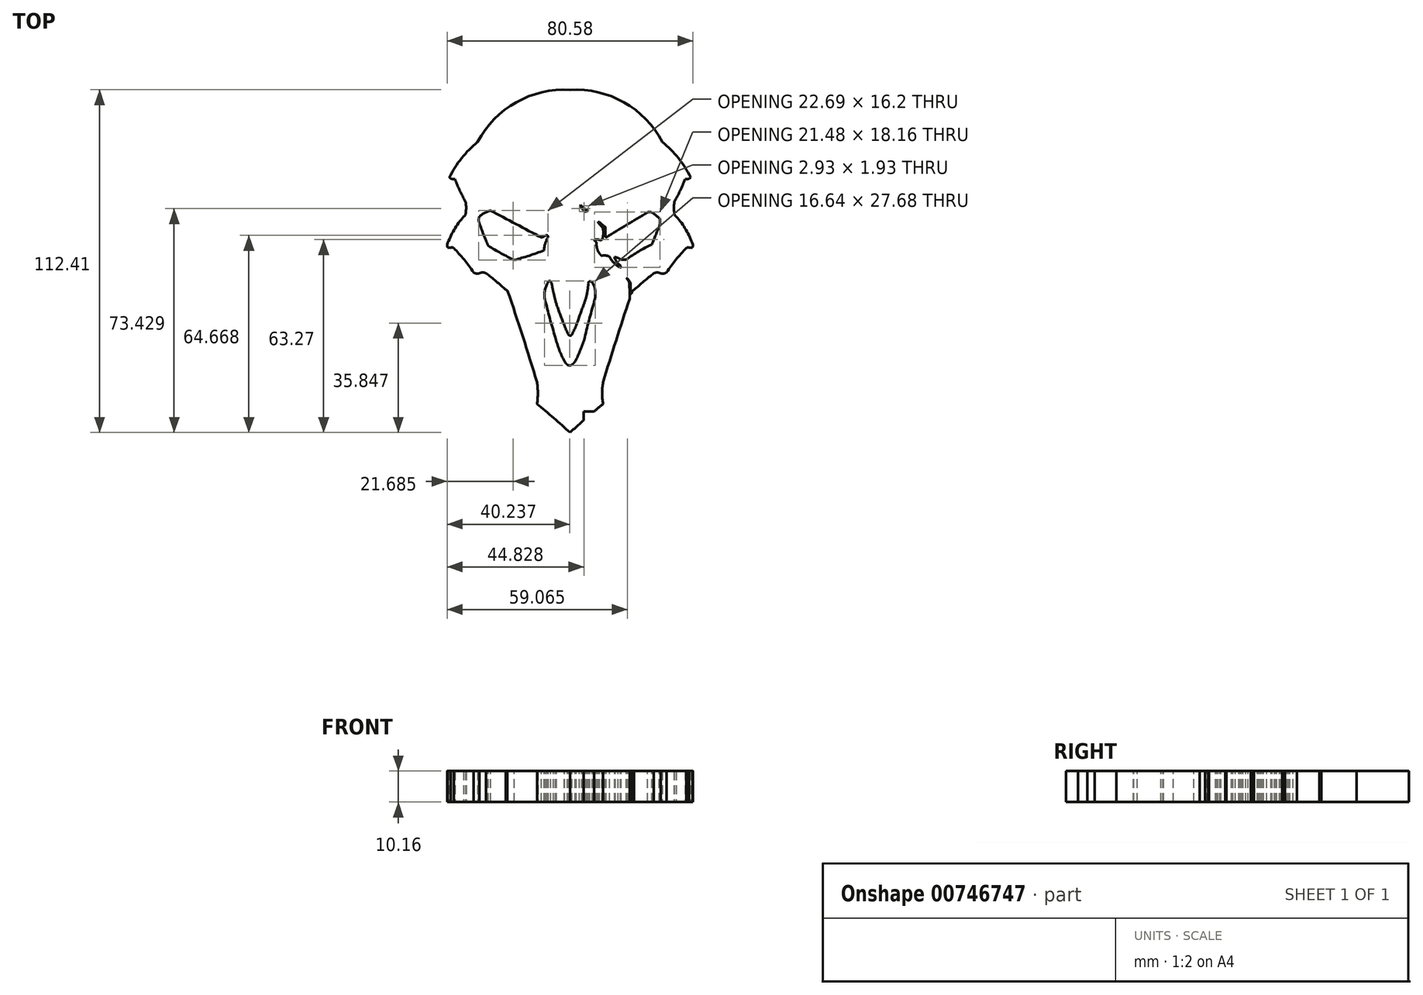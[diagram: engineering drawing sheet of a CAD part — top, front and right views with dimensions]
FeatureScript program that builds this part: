
annotation { "Feature Type Name" : "Feature", "Feature Type Description" : "" }
export const myFeature = defineFeature(function(context is Context, id is Id, definition is map)
    precondition{}
    {
        {
            var Q0;
            Q0=qCreatedBy(makeId("Top.planeOp"),FACE);
            var sketch = newSketch(context, id + "F0", { "sketchPlane" : qUnion([Q0])});
            skArc(sketch, "E0", {"start": v(-30.27, 46.68) * mm, "mid": v(-35.53, 41.4) * mm, "end": v(-39.5, 35.1) * mm});
            skArc(sketch, "E1", {"start": v(-39.5, 35.1) * mm, "mid": v(-38.7, 34.53) * mm, "end": v(-37.73, 34.53) * mm});
            skArc(sketch, "E2", {"start": v(-37.73, 34.53) * mm, "mid": v(-36.12, 30.74) * mm, "end": v(-34.24, 27.07) * mm});
            skArc(sketch, "E3", {"start": v(-34.24, 23.12) * mm, "mid": v(-34.05, 25.1) * mm, "end": v(-34.24, 27.07) * mm});
            skArc(sketch, "E4", {"start": v(-34.86, 22.24) * mm, "mid": v(-34.4, 22.58) * mm, "end": v(-34.24, 23.12) * mm});
            skArc(sketch, "E5", {"start": v(-38.1, 11.91) * mm, "mid": v(-38.57, 12.1) * mm, "end": v(-39.06, 12.04) * mm});
            skArc(sketch, "E6", {"start": v(-31.65, 3.94) * mm, "mid": v(-34.7, 8.07) * mm, "end": v(-38.1, 11.91) * mm});
            skArc(sketch, "E7", {"start": v(-34.86, 22.24) * mm, "mid": v(-38, 17.87) * mm, "end": v(-40.29, 12.99) * mm});
            skArc(sketch, "E8", {"start": v(-40.29, 12.99) * mm, "mid": v(-40.25, 12.5) * mm, "end": v(-40.1, 12.04) * mm});
            skArc(sketch, "E9", {"start": v(-40.1, 12.04) * mm, "mid": v(-39.58, 12.03) * mm, "end": v(-39.06, 12.04) * mm});
            skArc(sketch, "E10", {"start": v(-31.65, 3.94) * mm, "mid": v(-30.7, 3.53) * mm, "end": v(-29.68, 3.65) * mm});
            skArc(sketch, "E11", {"start": v(-27.5, 3.65) * mm, "mid": v(-28.59, 3.9) * mm, "end": v(-29.68, 3.65) * mm});
            skArc(sketch, "E12", {"start": v(-21.02, -1.81) * mm, "mid": v(-24.21, 0.97) * mm, "end": v(-27.5, 3.65) * mm});
            skArc(sketch, "E13", {"start": v(-20.5, -2.08) * mm, "mid": v(-20.73, -1.9) * mm, "end": v(-21.02, -1.81) * mm});
            skArc(sketch, "E14", {"start": v(-10.83, -32.15) * mm, "mid": v(-15.5, -17.06) * mm, "end": v(-20.5, -2.08) * mm});
            skArc(sketch, "E15", {"start": v(-10.83, -39.22) * mm, "mid": v(-10.55, -35.68) * mm, "end": v(-10.83, -32.15) * mm});
            skArc(sketch, "E16", {"start": v(0, -48.6) * mm, "mid": v(-5.35, -43.82) * mm, "end": v(-10.83, -39.22) * mm});
            skLineSegment(sketch, "E17", {"start": v(0, 63.77) * mm, "end": v(0, -48.6) * mm});
            skArc(sketch, "E18", {"start": v(0, 63.77) * mm, "mid": v(-17.65, 59.68) * mm, "end": v(-30.27, 46.68) * mm});
            skSolve(sketch);
        }
        {
            var Q0;
            Q0=qSketchRegion(id+"F0",true);
            extrude(context, id + "F1", {"entities" : qUnion([Q0]), "depth" : 10.16 * mm, "offsetDistance" : 25.4 * mm});
        }
        {
            var Q0;
            Q0=makeQuery(id+"F1.opExtrude","SWEPT_BODY",BODY,{"disambiguationData":[OSD([sQuery(id+"F0.wireOp",EDGE,"E0"),sQuery(id+"F0.wireOp",EDGE,"E1"),sQuery(id+"F0.wireOp",EDGE,"E2"),sQuery(id+"F0.wireOp",EDGE,"E3"),sQuery(id+"F0.wireOp",EDGE,"E4"),sQuery(id+"F0.wireOp",EDGE,"E5"),sQuery(id+"F0.wireOp",EDGE,"E6"),sQuery(id+"F0.wireOp",EDGE,"E7"),sQuery(id+"F0.wireOp",EDGE,"E8"),sQuery(id+"F0.wireOp",EDGE,"E9"),sQuery(id+"F0.wireOp",EDGE,"E10"),sQuery(id+"F0.wireOp",EDGE,"E11"),sQuery(id+"F0.wireOp",EDGE,"E12"),sQuery(id+"F0.wireOp",EDGE,"E13"),sQuery(id+"F0.wireOp",EDGE,"E14"),sQuery(id+"F0.wireOp",EDGE,"E15"),sQuery(id+"F0.wireOp",EDGE,"E16"),sQuery(id+"F0.wireOp",EDGE,"E17"),sQuery(id+"F0.wireOp",EDGE,"E18")])]});
            var Q1;
            Q1=qCreatedBy(makeId("Right.planeOp"),FACE);
            mirror(context, id + "F2", {"operationType" : NewBodyOperationType.ADD, "entities" : qUnion([Q0]), "mirrorPlane" : qUnion([Q1])});
        }
        {
            var Q0;
            {var subQ0=makeQuery(id+"F1.opExtrude","CAP_FACE",FACE,{"disambiguationData":[OSD([sQuery(id+"F0.wireOp",EDGE,"E0"),sQuery(id+"F0.wireOp",EDGE,"E1"),sQuery(id+"F0.wireOp",EDGE,"E2"),sQuery(id+"F0.wireOp",EDGE,"E3"),sQuery(id+"F0.wireOp",EDGE,"E4"),sQuery(id+"F0.wireOp",EDGE,"E5"),sQuery(id+"F0.wireOp",EDGE,"E6"),sQuery(id+"F0.wireOp",EDGE,"E7"),sQuery(id+"F0.wireOp",EDGE,"E8"),sQuery(id+"F0.wireOp",EDGE,"E9"),sQuery(id+"F0.wireOp",EDGE,"E10"),sQuery(id+"F0.wireOp",EDGE,"E11"),sQuery(id+"F0.wireOp",EDGE,"E12"),sQuery(id+"F0.wireOp",EDGE,"E13"),sQuery(id+"F0.wireOp",EDGE,"E14"),sQuery(id+"F0.wireOp",EDGE,"E15"),sQuery(id+"F0.wireOp",EDGE,"E16"),sQuery(id+"F0.wireOp",EDGE,"E17"),sQuery(id+"F0.wireOp",EDGE,"E18")])],"isStart":false});Q0=makeQuery(id+"F2.boolean.opBoolean","MERGE",FACE,{"derivedFrom":[subQ0,makeQuery(id+"F2.opPattern","COPY",FACE,{"derivedFrom":subQ0,"instanceName":"1"})]});}
            var sketch = newSketch(context, id + "F3", { "sketchPlane" : qUnion([Q0])});
            skArc(sketch, "E19", {"start": v(-26, 24.18) * mm, "mid": v(-17.72, 19.77) * mm, "end": v(-9.44, 15.37) * mm});
            skArc(sketch, "E20", {"start": v(-9.44, 15.37) * mm, "mid": v(-8.67, 15.65) * mm, "end": v(-7.94, 16.04) * mm});
            skArc(sketch, "E21", {"start": v(-26.76, 12.61) * mm, "mid": v(-22.58, 10.17) * mm, "end": v(-18.26, 7.98) * mm});
            skArc(sketch, "E22", {"start": v(-29.69, 20.03) * mm, "mid": v(-28.33, 16.28) * mm, "end": v(-26.76, 12.61) * mm});
            skArc(sketch, "E23", {"start": v(-29.69, 22.27) * mm, "mid": v(-29.95, 21.15) * mm, "end": v(-29.69, 20.03) * mm});
            skArc(sketch, "E24", {"start": v(-26, 24.18) * mm, "mid": v(-27.96, 23.44) * mm, "end": v(-29.69, 22.27) * mm});
            skArc(sketch, "E25", {"start": v(-7.58, 16.16) * mm, "mid": v(-7.77, 16.1) * mm, "end": v(-7.94, 16.04) * mm});
            skArc(sketch, "E26", {"start": v(-7.58, 16.16) * mm, "mid": v(-7.47, 16.14) * mm, "end": v(-7.35, 16.16) * mm});
            skArc(sketch, "E27", {"start": v(-7.28, 15.37) * mm, "mid": v(-7.26, 15.77) * mm, "end": v(-7.35, 16.16) * mm});
            skArc(sketch, "E28", {"start": v(-7.28, 15.37) * mm, "mid": v(-8.16, 13.31) * mm, "end": v(-8.55, 11.1) * mm});
            skArc(sketch, "E29", {"start": v(-18.26, 7.98) * mm, "mid": v(-13.36, 9.42) * mm, "end": v(-8.55, 11.1) * mm});
            skSolve(sketch);
        }
        {
            var Q0;
            Q0=qSketchRegion(id+"F3",true);
            extrude(context, id + "F4", {"entities" : qUnion([Q0]), "operationType" : NewBodyOperationType.REMOVE, "oppositeDirection" : true, "depth" : 25.4 * mm, "offsetDistance" : 25.4 * mm});
        }
        {
            var Q0;
            {var subQ0=makeQuery(id+"F1.opExtrude","CAP_FACE",FACE,{"disambiguationData":[OSD([sQuery(id+"F0.wireOp",EDGE,"E0"),sQuery(id+"F0.wireOp",EDGE,"E1"),sQuery(id+"F0.wireOp",EDGE,"E2"),sQuery(id+"F0.wireOp",EDGE,"E3"),sQuery(id+"F0.wireOp",EDGE,"E4"),sQuery(id+"F0.wireOp",EDGE,"E5"),sQuery(id+"F0.wireOp",EDGE,"E6"),sQuery(id+"F0.wireOp",EDGE,"E7"),sQuery(id+"F0.wireOp",EDGE,"E8"),sQuery(id+"F0.wireOp",EDGE,"E9"),sQuery(id+"F0.wireOp",EDGE,"E10"),sQuery(id+"F0.wireOp",EDGE,"E11"),sQuery(id+"F0.wireOp",EDGE,"E12"),sQuery(id+"F0.wireOp",EDGE,"E13"),sQuery(id+"F0.wireOp",EDGE,"E14"),sQuery(id+"F0.wireOp",EDGE,"E15"),sQuery(id+"F0.wireOp",EDGE,"E16"),sQuery(id+"F0.wireOp",EDGE,"E17"),sQuery(id+"F0.wireOp",EDGE,"E18")])],"isStart":false});Q0=makeQuery(id+"F2.boolean.opBoolean","MERGE",FACE,{"derivedFrom":[subQ0,makeQuery(id+"F2.opPattern","COPY",FACE,{"derivedFrom":subQ0,"instanceName":"1"})]});}
            var sketch = newSketch(context, id + "F5", { "sketchPlane" : qUnion([Q0])});
            skArc(sketch, "E30", {"start": v(25.42, 23.61) * mm, "mid": v(18.6, 19.55) * mm, "end": v(11.87, 15.37) * mm});
            skArc(sketch, "E31", {"start": v(26.78, 23.61) * mm, "mid": v(26.1, 23.76) * mm, "end": v(25.42, 23.61) * mm});
            skArc(sketch, "E32", {"start": v(29.26, 21.73) * mm, "mid": v(28.05, 22.71) * mm, "end": v(26.78, 23.61) * mm});
            skArc(sketch, "E33", {"start": v(29.5, 21.39) * mm, "mid": v(29.4, 21.57) * mm, "end": v(29.26, 21.73) * mm});
            skArc(sketch, "E34", {"start": v(29.5, 19.76) * mm, "mid": v(29.51, 20.58) * mm, "end": v(29.5, 21.39) * mm});
            skArc(sketch, "E35", {"start": v(26.78, 13.08) * mm, "mid": v(28.17, 16.4) * mm, "end": v(29.5, 19.76) * mm});
            skArc(sketch, "E36", {"start": v(26.78, 13.08) * mm, "mid": v(22.49, 10.8) * mm, "end": v(18.43, 8.13) * mm});
            skArc(sketch, "E37", {"start": v(16.8, 8.13) * mm, "mid": v(17.62, 8.07) * mm, "end": v(18.43, 8.13) * mm});
            skArc(sketch, "E38", {"start": v(16.8, 8.13) * mm, "mid": v(15.76, 8.64) * mm, "end": v(14.65, 8.96) * mm});
            skArc(sketch, "E39", {"start": v(12.98, 9) * mm, "mid": v(13.7, 7.88) * mm, "end": v(14.58, 6.88) * mm});
            skArc(sketch, "E40", {"start": v(12.1, 9.4) * mm, "mid": v(11.24, 9.46) * mm, "end": v(10.38, 9.4) * mm});
            skArc(sketch, "E41", {"start": v(9.5, 10.35) * mm, "mid": v(9.88, 9.82) * mm, "end": v(10.38, 9.4) * mm});
            skArc(sketch, "E42", {"start": v(8.7, 13.2) * mm, "mid": v(8.88, 11.72) * mm, "end": v(9.5, 10.35) * mm});
            skArc(sketch, "E43", {"start": v(8.7, 13.2) * mm, "mid": v(8.63, 13.72) * mm, "end": v(8.25, 14.08) * mm});
            skArc(sketch, "E44", {"start": v(8.07, 14.36) * mm, "mid": v(8.15, 14.2) * mm, "end": v(8.25, 14.08) * mm});
            skArc(sketch, "E45", {"start": v(8.07, 14.73) * mm, "mid": v(8.03, 14.54) * mm, "end": v(8.07, 14.36) * mm});
            skArc(sketch, "E46", {"start": v(14.9, 8.09) * mm, "mid": v(15.57, 7) * mm, "end": v(16.55, 6.16) * mm});
            skArc(sketch, "E47", {"start": v(16.55, 6.16) * mm, "mid": v(16.6, 5.84) * mm, "end": v(16.84, 5.6) * mm});
            skArc(sketch, "E48", {"start": v(15.76, 5.9) * mm, "mid": v(16.27, 5.66) * mm, "end": v(16.84, 5.6) * mm});
            skArc(sketch, "E49", {"start": v(14.58, 6.88) * mm, "mid": v(15.14, 6.35) * mm, "end": v(15.76, 5.9) * mm});
            skArc(sketch, "E50", {"start": v(10.45, 14.6) * mm, "mid": v(10.58, 14.76) * mm, "end": v(10.64, 14.94) * mm});
            skArc(sketch, "E51", {"start": v(10.64, 14.94) * mm, "mid": v(10.87, 16.03) * mm, "end": v(10.9, 17.14) * mm});
            skArc(sketch, "E52", {"start": v(10.9, 17.14) * mm, "mid": v(10.85, 17.89) * mm, "end": v(10.64, 18.61) * mm});
            skArc(sketch, "E53", {"start": v(10.64, 18.61) * mm, "mid": v(10, 19.4) * mm, "end": v(9.28, 20.13) * mm});
            skArc(sketch, "E54", {"start": v(9.2, 20.42) * mm, "mid": v(9.22, 20.27) * mm, "end": v(9.28, 20.13) * mm});
            skArc(sketch, "E55", {"start": v(9.2, 20.42) * mm, "mid": v(9.46, 20.35) * mm, "end": v(9.72, 20.42) * mm});
            skArc(sketch, "E56", {"start": v(9.72, 20.42) * mm, "mid": v(10.53, 19.58) * mm, "end": v(11.48, 18.92) * mm});
            skArc(sketch, "E57", {"start": v(11.59, 18.76) * mm, "mid": v(11.55, 18.85) * mm, "end": v(11.48, 18.92) * mm});
            skArc(sketch, "E58", {"start": v(11.74, 15.48) * mm, "mid": v(11.78, 15.4) * mm, "end": v(11.87, 15.37) * mm});
            skArc(sketch, "E59", {"start": v(11.59, 18.76) * mm, "mid": v(11.54, 17.12) * mm, "end": v(11.74, 15.48) * mm});
            skArc(sketch, "E60", {"start": v(9.51, 14.6) * mm, "mid": v(9.98, 14.5) * mm, "end": v(10.45, 14.6) * mm});
            skArc(sketch, "E61", {"start": v(9.51, 14.6) * mm, "mid": v(9.27, 14.67) * mm, "end": v(9.02, 14.7) * mm});
            skArc(sketch, "E62", {"start": v(8.48, 14.71) * mm, "mid": v(8.75, 14.65) * mm, "end": v(9.02, 14.7) * mm});
            skArc(sketch, "E63", {"start": v(8.07, 14.73) * mm, "mid": v(8.27, 14.69) * mm, "end": v(8.48, 14.71) * mm});
            skArc(sketch, "E64", {"start": v(14.65, 8.96) * mm, "mid": v(14.6, 8.78) * mm, "end": v(14.65, 8.6) * mm});
            skArc(sketch, "E65", {"start": v(14.65, 8.6) * mm, "mid": v(14.76, 8.34) * mm, "end": v(14.9, 8.09) * mm});
            skArc(sketch, "E66", {"start": v(12.98, 9) * mm, "mid": v(12.57, 9.26) * mm, "end": v(12.1, 9.4) * mm});
            skSolve(sketch);
        }
        {
            var Q0;
            Q0=qSketchRegion(id+"F5",true);
            extrude(context, id + "F6", {"entities" : qUnion([Q0]), "operationType" : NewBodyOperationType.REMOVE, "oppositeDirection" : true, "depth" : 25.4 * mm, "offsetDistance" : 25.4 * mm});
        }
        {
            var Q0;
            Q0=qSketchRegion(id+"F5",true);
            extrude(context, id + "F7", {"entities" : qUnion([Q0]), "operationType" : NewBodyOperationType.REMOVE, "oppositeDirection" : true, "depth" : 25.4 * mm, "offsetDistance" : 25.4 * mm});
        }
        {
            var Q0;
            {var subQ0=makeQuery(id+"F1.opExtrude","CAP_FACE",FACE,{"disambiguationData":[OSD([sQuery(id+"F0.wireOp",EDGE,"E0"),sQuery(id+"F0.wireOp",EDGE,"E1"),sQuery(id+"F0.wireOp",EDGE,"E2"),sQuery(id+"F0.wireOp",EDGE,"E3"),sQuery(id+"F0.wireOp",EDGE,"E4"),sQuery(id+"F0.wireOp",EDGE,"E5"),sQuery(id+"F0.wireOp",EDGE,"E6"),sQuery(id+"F0.wireOp",EDGE,"E7"),sQuery(id+"F0.wireOp",EDGE,"E8"),sQuery(id+"F0.wireOp",EDGE,"E9"),sQuery(id+"F0.wireOp",EDGE,"E10"),sQuery(id+"F0.wireOp",EDGE,"E11"),sQuery(id+"F0.wireOp",EDGE,"E12"),sQuery(id+"F0.wireOp",EDGE,"E13"),sQuery(id+"F0.wireOp",EDGE,"E14"),sQuery(id+"F0.wireOp",EDGE,"E15"),sQuery(id+"F0.wireOp",EDGE,"E16"),sQuery(id+"F0.wireOp",EDGE,"E17"),sQuery(id+"F0.wireOp",EDGE,"E18")])],"isStart":false});Q0=makeQuery(id+"F2.boolean.opBoolean","MERGE",FACE,{"derivedFrom":[subQ0,makeQuery(id+"F2.opPattern","COPY",FACE,{"derivedFrom":subQ0,"instanceName":"1"})]});}
            var sketch = newSketch(context, id + "F8", { "sketchPlane" : qUnion([Q0])});
            skArc(sketch, "E67", {"start": v(19.58, -4.75) * mm, "mid": v(19.54, -2.14) * mm, "end": v(19.42, 0.46) * mm});
            skArc(sketch, "E68", {"start": v(19.42, 0.46) * mm, "mid": v(19.15, 1.16) * mm, "end": v(18.68, 1.76) * mm});
            skArc(sketch, "E69", {"start": v(18.68, 2) * mm, "mid": v(18.66, 1.88) * mm, "end": v(18.68, 1.76) * mm});
            skArc(sketch, "E70", {"start": v(18.75, 2.17) * mm, "mid": v(18.7, 2.1) * mm, "end": v(18.68, 2) * mm});
            skArc(sketch, "E71", {"start": v(18.75, 2.17) * mm, "mid": v(18.8, 1.91) * mm, "end": v(19, 1.74) * mm});
            skArc(sketch, "E72", {"start": v(19.78, 0.52) * mm, "mid": v(19.41, 1.15) * mm, "end": v(19, 1.74) * mm});
            skArc(sketch, "E73", {"start": v(19.78, 0.52) * mm, "mid": v(19.85, -1.26) * mm, "end": v(20.03, -3.02) * mm});
            skArc(sketch, "E74", {"start": v(20.03, -3.02) * mm, "mid": v(20.05, -3.06) * mm, "end": v(20.08, -3.08) * mm});
            skArc(sketch, "E75", {"start": v(20.08, -3.08) * mm, "mid": v(20.16, -3.07) * mm, "end": v(20.22, -3) * mm});
            skArc(sketch, "E76", {"start": v(19.58, -4.75) * mm, "mid": v(24.58, -5.6) * mm, "end": v(20.22, -3) * mm});
            skSolve(sketch);
        }
        {
            var Q0;
            {var subQ0=makeQuery(id+"F1.opExtrude","CAP_FACE",FACE,{"disambiguationData":[OSD([sQuery(id+"F0.wireOp",EDGE,"E0"),sQuery(id+"F0.wireOp",EDGE,"E1"),sQuery(id+"F0.wireOp",EDGE,"E2"),sQuery(id+"F0.wireOp",EDGE,"E3"),sQuery(id+"F0.wireOp",EDGE,"E4"),sQuery(id+"F0.wireOp",EDGE,"E5"),sQuery(id+"F0.wireOp",EDGE,"E6"),sQuery(id+"F0.wireOp",EDGE,"E7"),sQuery(id+"F0.wireOp",EDGE,"E8"),sQuery(id+"F0.wireOp",EDGE,"E9"),sQuery(id+"F0.wireOp",EDGE,"E10"),sQuery(id+"F0.wireOp",EDGE,"E11"),sQuery(id+"F0.wireOp",EDGE,"E12"),sQuery(id+"F0.wireOp",EDGE,"E13"),sQuery(id+"F0.wireOp",EDGE,"E14"),sQuery(id+"F0.wireOp",EDGE,"E15"),sQuery(id+"F0.wireOp",EDGE,"E16"),sQuery(id+"F0.wireOp",EDGE,"E17"),sQuery(id+"F0.wireOp",EDGE,"E18")])],"isStart":false});Q0=makeQuery(id+"F2.boolean.opBoolean","MERGE",FACE,{"derivedFrom":[subQ0,makeQuery(id+"F2.opPattern","COPY",FACE,{"derivedFrom":subQ0,"instanceName":"1"})]});}
            var sketch = newSketch(context, id + "F9", { "sketchPlane" : qUnion([Q0])});
            skArc(sketch, "E77", {"start": v(3.88, 25.76) * mm, "mid": v(4.36, 25.2) * mm, "end": v(4.93, 24.73) * mm});
            skArc(sketch, "E78", {"start": v(4.93, 24.73) * mm, "mid": v(5.45, 24.54) * mm, "end": v(6, 24.5) * mm});
            skArc(sketch, "E79", {"start": v(4.68, 23.9) * mm, "mid": v(4.97, 23.88) * mm, "end": v(5.26, 23.9) * mm});
            skArc(sketch, "E80", {"start": v(4.68, 23.9) * mm, "mid": v(3.93, 24.9) * mm, "end": v(3.07, 25.8) * mm});
            skArc(sketch, "E81", {"start": v(3.07, 25.8) * mm, "mid": v(3.47, 25.74) * mm, "end": v(3.88, 25.76) * mm});
            skArc(sketch, "E82", {"start": v(6, 24.5) * mm, "mid": v(5.8, 24.24) * mm, "end": v(5.69, 23.95) * mm});
            skArc(sketch, "E83", {"start": v(5.69, 23.95) * mm, "mid": v(5.47, 23.94) * mm, "end": v(5.26, 23.9) * mm});
            skSolve(sketch);
        }
        {
            var Q0;
            Q0=qSketchRegion(id+"F9",true);
            extrude(context, id + "F10", {"entities" : qUnion([Q0]), "operationType" : NewBodyOperationType.REMOVE, "oppositeDirection" : true, "depth" : 25.4 * mm, "offsetDistance" : 25.4 * mm});
        }
        {
            var Q0;
            {var subQ20=sQuery(id+"F8.wireOp",EDGE,"E67");Q0=makeQuery(id+"F8.imprint","IMPRINT",FACE,{"disambiguationData":[TD([[makeQuery(id+"F8.imprint","IMPRINT",EDGE,{"derivedFrom":subQ20}),1.0]])]});}
            var sketch = newSketch(context, id + "F11", { "sketchPlane" : qUnion([Q0])});
            skArc(sketch, "E84", {"start": v(-6.35, 0.89) * mm, "mid": v(-6.69, 1.1) * mm, "end": v(-7.05, 0.93) * mm});
            skArc(sketch, "E85", {"start": v(-7.05, 0.93) * mm, "mid": v(-8.21, -1.83) * mm, "end": v(-8.25, -4.82) * mm});
            skArc(sketch, "E86", {"start": v(-8.25, -4.82) * mm, "mid": v(-6.62, -11.16) * mm, "end": v(-4.78, -17.44) * mm});
            skArc(sketch, "E87", {"start": v(-4.78, -17.44) * mm, "mid": v(-3.54, -21.47) * mm, "end": v(-1.75, -25.28) * mm});
            skArc(sketch, "E88", {"start": v(-1.75, -25.28) * mm, "mid": v(-1.37, -25.86) * mm, "end": v(-0.9, -26.35) * mm});
            skArc(sketch, "E89", {"start": v(-0.9, -26.35) * mm, "mid": v(-0.13, -26.59) * mm, "end": v(0.64, -26.35) * mm});
            skArc(sketch, "E90", {"start": v(0.64, -26.35) * mm, "mid": v(1.2, -25.84) * mm, "end": v(1.7, -25.28) * mm});
            skArc(sketch, "E91", {"start": v(1.7, -25.28) * mm, "mid": v(3.44, -21.43) * mm, "end": v(4.85, -17.44) * mm});
            skArc(sketch, "E92", {"start": v(8.19, -4.82) * mm, "mid": v(6.4, -11.1) * mm, "end": v(4.85, -17.44) * mm});
            skArc(sketch, "E93", {"start": v(8.19, -4.82) * mm, "mid": v(8.27, -3.16) * mm, "end": v(8.19, -1.5) * mm});
            skArc(sketch, "E94", {"start": v(8.19, -1.5) * mm, "mid": v(7.82, -0.38) * mm, "end": v(7.27, 0.67) * mm});
            skArc(sketch, "E95", {"start": v(7.27, 0.67) * mm, "mid": v(6.93, 0.9) * mm, "end": v(6.55, 1.01) * mm});
            skArc(sketch, "E96", {"start": v(5.65, -2.47) * mm, "mid": v(5.9, -1.06) * mm, "end": v(5.93, 0.36) * mm});
            skArc(sketch, "E97", {"start": v(4.5, -6.68) * mm, "mid": v(5.18, -4.6) * mm, "end": v(5.65, -2.47) * mm});
            skArc(sketch, "E98", {"start": v(4.5, -6.68) * mm, "mid": v(3.23, -10.02) * mm, "end": v(2.08, -13.4) * mm});
            skArc(sketch, "E99", {"start": v(0.57, -16.55) * mm, "mid": v(1.35, -14.98) * mm, "end": v(2.08, -13.4) * mm});
            skArc(sketch, "E100", {"start": v(-0.45, -16.55) * mm, "mid": v(0.06, -16.81) * mm, "end": v(0.57, -16.55) * mm});
            skArc(sketch, "E101", {"start": v(-1.88, -13.4) * mm, "mid": v(-1.23, -15) * mm, "end": v(-0.45, -16.55) * mm});
            skArc(sketch, "E102", {"start": v(-4.4, -6.68) * mm, "mid": v(-3.18, -10.05) * mm, "end": v(-1.88, -13.4) * mm});
            skArc(sketch, "E103", {"start": v(-5.5, -2.47) * mm, "mid": v(-4.97, -4.58) * mm, "end": v(-4.4, -6.68) * mm});
            skArc(sketch, "E104", {"start": v(-5.97, -0.02) * mm, "mid": v(-5.74, -1.24) * mm, "end": v(-5.5, -2.47) * mm});
            skArc(sketch, "E105", {"start": v(-5.97, -0.02) * mm, "mid": v(-6.1, 0.46) * mm, "end": v(-6.35, 0.89) * mm});
            skArc(sketch, "E106", {"start": v(6.55, 1.01) * mm, "mid": v(6.15, 0.77) * mm, "end": v(5.93, 0.36) * mm});
            skSolve(sketch);
        }
        {
            var Q0;
            Q0=qSketchRegion(id+"F11",true);
            extrude(context, id + "F12", {"entities" : qUnion([Q0]), "operationType" : NewBodyOperationType.REMOVE, "oppositeDirection" : true, "depth" : 25.4 * mm, "offsetDistance" : 25.4 * mm});
        }
        {
            var Q0;
            {var subQ0=makeQuery(id+"F1.opExtrude","CAP_FACE",FACE,{"disambiguationData":[OSD([sQuery(id+"F0.wireOp",EDGE,"E0"),sQuery(id+"F0.wireOp",EDGE,"E1"),sQuery(id+"F0.wireOp",EDGE,"E2"),sQuery(id+"F0.wireOp",EDGE,"E3"),sQuery(id+"F0.wireOp",EDGE,"E4"),sQuery(id+"F0.wireOp",EDGE,"E5"),sQuery(id+"F0.wireOp",EDGE,"E6"),sQuery(id+"F0.wireOp",EDGE,"E7"),sQuery(id+"F0.wireOp",EDGE,"E8"),sQuery(id+"F0.wireOp",EDGE,"E9"),sQuery(id+"F0.wireOp",EDGE,"E10"),sQuery(id+"F0.wireOp",EDGE,"E11"),sQuery(id+"F0.wireOp",EDGE,"E12"),sQuery(id+"F0.wireOp",EDGE,"E13"),sQuery(id+"F0.wireOp",EDGE,"E14"),sQuery(id+"F0.wireOp",EDGE,"E15"),sQuery(id+"F0.wireOp",EDGE,"E16"),sQuery(id+"F0.wireOp",EDGE,"E17"),sQuery(id+"F0.wireOp",EDGE,"E18")])],"isStart":false});Q0=makeQuery(id+"F2.boolean.opBoolean","MERGE",FACE,{"derivedFrom":[subQ0,makeQuery(id+"F2.opPattern","COPY",FACE,{"derivedFrom":subQ0,"instanceName":"1"})]});}
            var sketch = newSketch(context, id + "F13", { "sketchPlane" : qUnion([Q0])});
            skLineSegment(sketch, "E107", {"start": v(4.41, -44.64) * mm, "end": v(4.41, -41.69) * mm});
            skLineSegment(sketch, "E108", {"start": v(4.41, -41.69) * mm, "end": v(7.85, -41.69) * mm});
            skArc(sketch, "E109", {"start": v(4.41, -44.64) * mm, "mid": v(7.42, -44.66) * mm, "end": v(7.85, -41.69) * mm});
            skSolve(sketch);
        }
        {
            var Q0;
            Q0=qSketchRegion(id+"F13",true);
            extrude(context, id + "F14", {"entities" : qUnion([Q0]), "operationType" : NewBodyOperationType.REMOVE, "oppositeDirection" : true, "depth" : 25.4 * mm, "offsetDistance" : 25.4 * mm});
        }
        {
            var Q0;
            Q0=qSketchRegion(id+"F8",true);
            extrude(context, id + "F15", {"entities" : qUnion([Q0]), "operationType" : NewBodyOperationType.REMOVE, "oppositeDirection" : true, "depth" : 25.4 * mm, "offsetDistance" : 25.4 * mm});
        }
    });
